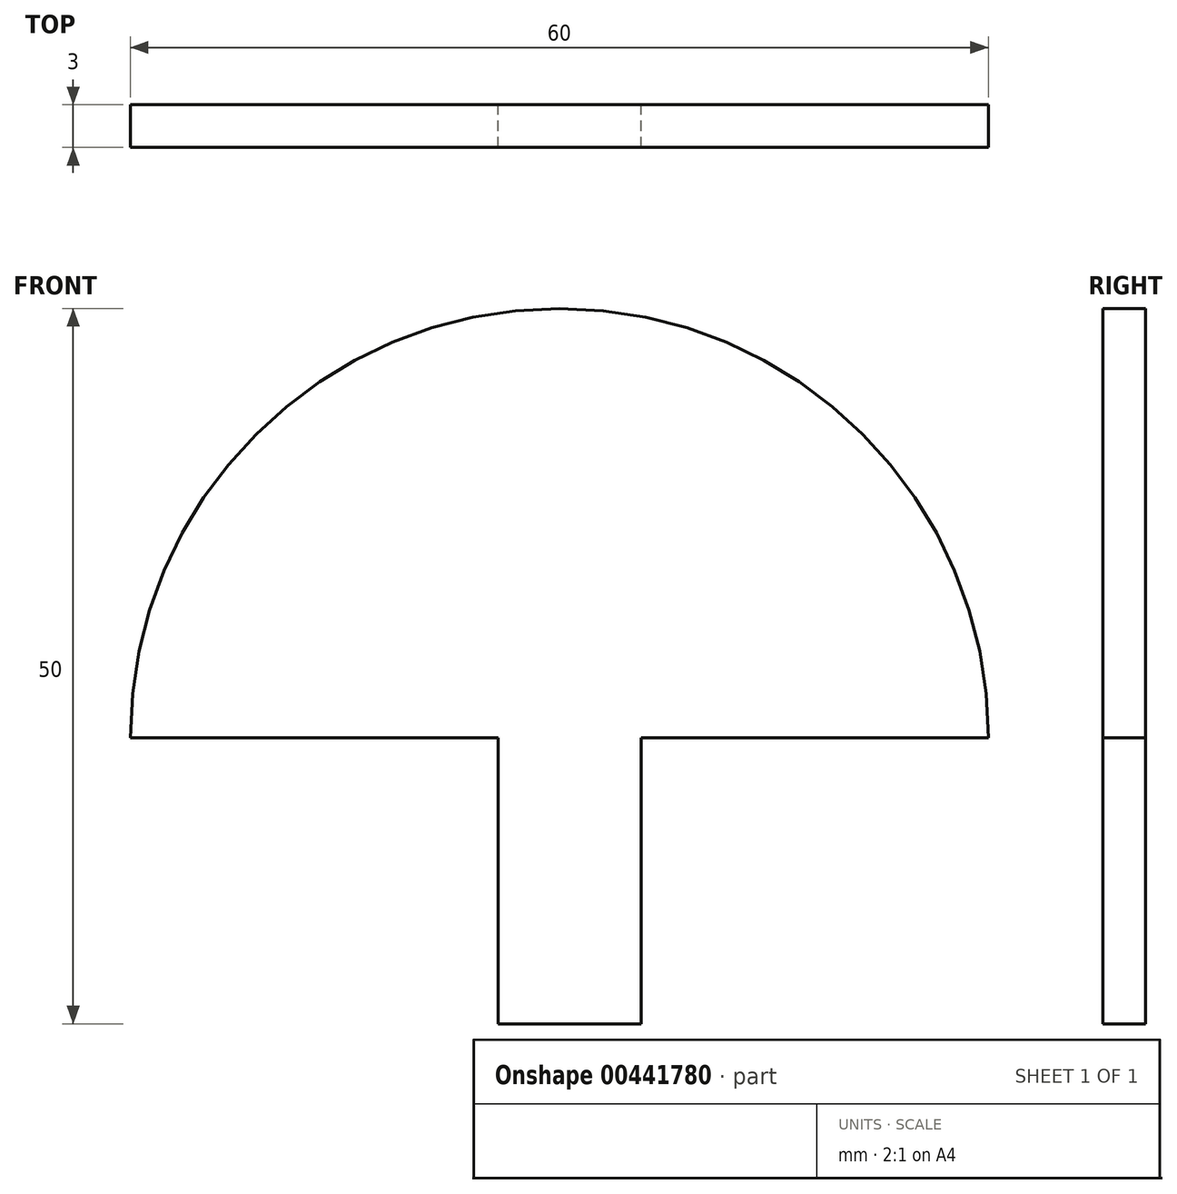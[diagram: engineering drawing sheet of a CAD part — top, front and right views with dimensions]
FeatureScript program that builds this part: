
annotation { "Feature Type Name" : "Feature", "Feature Type Description" : "" }
export const myFeature = defineFeature(function(context is Context, id is Id, definition is map)
    precondition{}
    {
        {
            var Q0;
            Q0=qCreatedBy(makeId("Front.planeOp"),FACE);
            var sketch = newSketch(context, id + "F0", { "sketchPlane" : qUnion([Q0])});
            skLineSegment(sketch, "E0.bottom", {"start": v(0, 0) * mm, "end": v(-10, 0) * mm});
            skLineSegment(sketch, "E0.left", {"start": v(0, 0) * mm, "end": v(0, 20) * mm});
            skLineSegment(sketch, "E0.right", {"start": v(-10, 0) * mm, "end": v(-10, 20) * mm});
            skLineSegment(sketch, "E1", {"start": v(-10, 20) * mm, "end": v(-35.71, 20) * mm});
            skLineSegment(sketch, "E2", {"start": v(-35.71, 20) * mm, "end": v(-10, 20) * mm});
            skArc(sketch, "E3", {"start": v(24.29, 20) * mm, "mid": v(-5.71, 50) * mm, "end": v(-35.71, 20) * mm});
            skLineSegment(sketch, "E4.trimOffspring", {"start": v(0, 20) * mm, "end": v(24.29, 20) * mm});
            skSolve(sketch);
        }
        {
            var Q0;
            Q0=makeQuery(id+"F0.imprint","IMPRINT",FACE,{"disambiguationData":[TD([[makeQuery(id+"F0.imprint","IMPRINT",EDGE,{"derivedFrom":sQuery(id+"F0.wireOp",EDGE,"E0.bottom")}),-1.0]])]});
            extrude(context, id + "F1", {"entities" : qUnion([Q0]), "depth" : 3 * mm});
        }
    });
